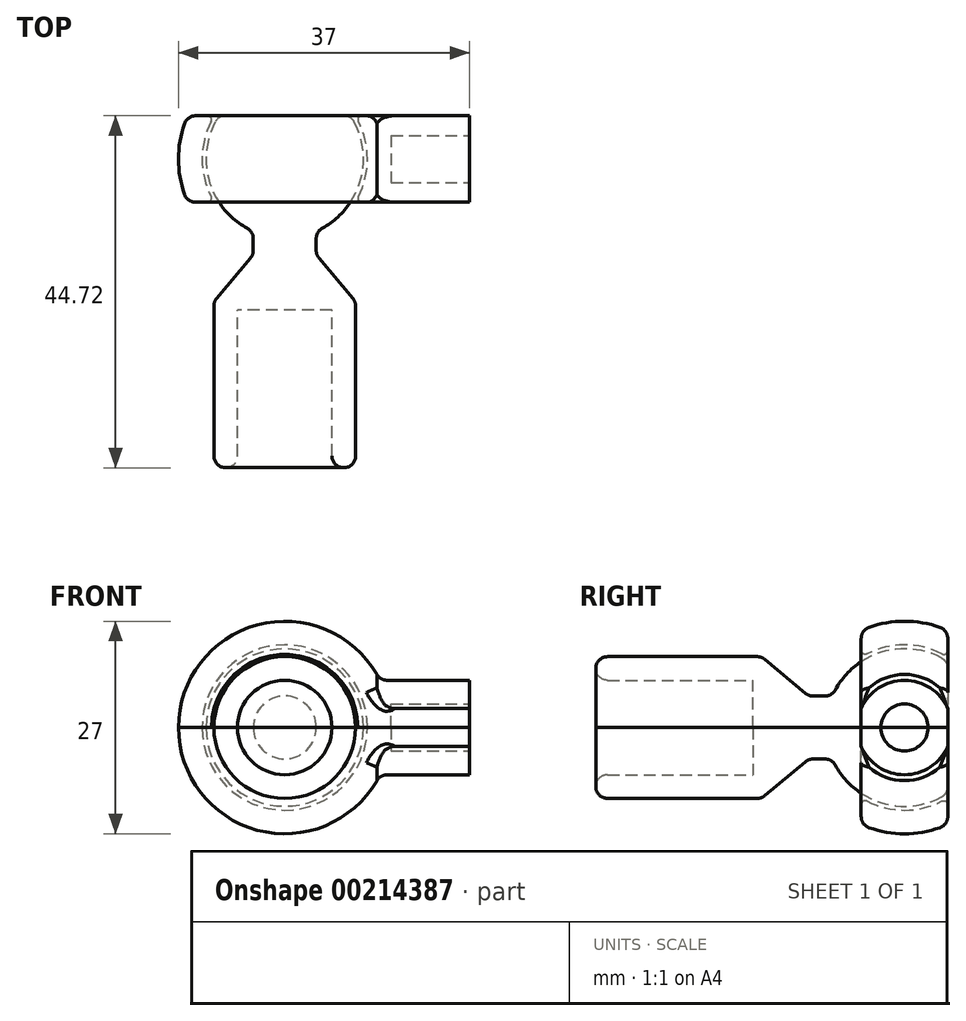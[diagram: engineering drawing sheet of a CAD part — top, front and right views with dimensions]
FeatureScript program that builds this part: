
annotation { "Feature Type Name" : "Feature", "Feature Type Description" : "" }
export const myFeature = defineFeature(function(context is Context, id is Id, definition is map)
    precondition{}
    {
        {
            var Q0;
            Q0=qCreatedBy(makeId("Top.planeOp"),FACE);
            var sketch = newSketch(context, id + "F0", { "sketchPlane" : qUnion([Q0])});
            skArc(sketch, "E0", {"start": v(-8.35, 5.5) * mm, "mid": v(-9.59, -2.84) * mm, "end": v(-4, -9.17) * mm});
            skLineSegment(sketch, "E1", {"start": v(-8.35, 5.5) * mm, "end": v(0, 5.5) * mm});
            skLineSegment(sketch, "E2", {"start": v(0, 14.58) * mm, "end": v(0, -45.08) * mm, "construction": true});
            skLineSegment(sketch, "E3", {"start": v(-4, -9.17) * mm, "end": v(-4, -12.17) * mm});
            skLineSegment(sketch, "E4", {"start": v(-4, -12.17) * mm, "end": v(-9, -18.12) * mm});
            skLineSegment(sketch, "E5", {"start": v(-9, -18.12) * mm, "end": v(-9, -39.22) * mm});
            skLineSegment(sketch, "E6", {"start": v(-9, -39.22) * mm, "end": v(-6, -39.22) * mm});
            skLineSegment(sketch, "E7", {"start": v(-6, -39.22) * mm, "end": v(-6, -19.22) * mm});
            skLineSegment(sketch, "E8", {"start": v(-6, -19.22) * mm, "end": v(0, -19.22) * mm});
            skLineSegment(sketch, "E9", {"start": v(-6, -19.22) * mm, "end": v(-8.3, -17.29) * mm, "construction": true});
            skPoint(sketch, "E10.MirrorCS.end.orphan", {"position": v(0, -19.22) * mm});
            skPoint(sketch, "E10.MirrorCS.start.orphan", {"position": v(6, -19.22) * mm});
            skPoint(sketch, "E11.MirrorCS.start.orphan", {"position": v(6, -39.22) * mm});
            skPoint(sketch, "E12.MirrorCS.start.orphan", {"position": v(9, -39.22) * mm});
            skPoint(sketch, "E13.MirrorCS.start.orphan", {"position": v(9, -18.12) * mm});
            skPoint(sketch, "E14.MirrorCS.start.orphan", {"position": v(4, -12.17) * mm});
            skPoint(sketch, "E15.MirrorCS.start.orphan", {"position": v(4, -9.17) * mm});
            skPoint(sketch, "E16.MirrorCS.start.orphan", {"position": v(8.35, 5.5) * mm});
            skPoint(sketch, "E17.MirrorCS.end.orphan", {"position": v(0, 5.5) * mm});
            skLineSegment(sketch, "E18", {"start": v(0, -19.22) * mm, "end": v(0, 5.5) * mm});
            skSolve(sketch);
        }
        {
            var Q0;
            Q0 = qSketchRegion(id + "F0", true);
            var Q1;
            Q1=sQuery(id+"F0.wireOp",EDGE,"E2");
            revolve(context, id + "F1", {"entities" : qUnion([Q0]), "axis" : qUnion([Q1]), "revolveType" : RevolveType.ONE_DIRECTION, "angle" : 180 * degree});
        }
        {
            var Q0;
            Q0=makeQuery(id+"F1.opRevolve","SWEPT_EDGE",EDGE,{"disambiguationData":[OSD([sQuery(id+"F0.wireOp",EDGE,"E0"),sQuery(id+"F0.wireOp",EDGE,"E3")])]});
            var Q1;
            Q1=makeQuery(id+"F1.opRevolve","SWEPT_EDGE",EDGE,{"disambiguationData":[OSD([sQuery(id+"F0.wireOp",EDGE,"E3"),sQuery(id+"F0.wireOp",EDGE,"E4")])]});
            var Q2;
            Q2=makeQuery(id+"F1.opRevolve","SWEPT_EDGE",EDGE,{"disambiguationData":[OSD([sQuery(id+"F0.wireOp",EDGE,"E4"),sQuery(id+"F0.wireOp",EDGE,"E5")])]});
            var Q3;
            Q3=makeQuery(id+"F1.opRevolve","SWEPT_EDGE",EDGE,{"disambiguationData":[OSD([sQuery(id+"F0.wireOp",EDGE,"E5"),sQuery(id+"F0.wireOp",EDGE,"E6")])]});
            var Q4;
            Q4=makeQuery(id+"F1.opRevolve","SWEPT_EDGE",EDGE,{"disambiguationData":[OSD([sQuery(id+"F0.wireOp",EDGE,"E6"),sQuery(id+"F0.wireOp",EDGE,"E7")])]});
            var Q5;
            Q5=makeQuery(id+"F1.opRevolve","SWEPT_EDGE",EDGE,{"disambiguationData":[OSD([sQuery(id+"F0.wireOp",EDGE,"E0"),sQuery(id+"F0.wireOp",EDGE,"E1")])]});
            fillet(context, id + "F2", {"entities" : qUnion([Q0, Q1, Q2, Q3, Q4, Q5]), "radius" : 1.5 * mm, "tangentPropagation" : true, "allowEdgeOverflow" : false});
        }
        {
            var Q0;
            Q0=makeQuery(id+"F1.opRevolve","CAP_FACE",FACE,{"disambiguationData":[OSD([sQuery(id+"F0.wireOp",EDGE,"E0"),sQuery(id+"F0.wireOp",EDGE,"E1"),sQuery(id+"F0.wireOp",EDGE,"E3"),sQuery(id+"F0.wireOp",EDGE,"E4"),sQuery(id+"F0.wireOp",EDGE,"E5"),sQuery(id+"F0.wireOp",EDGE,"E6"),sQuery(id+"F0.wireOp",EDGE,"E7"),sQuery(id+"F0.wireOp",EDGE,"E8"),sQuery(id+"F0.wireOp",EDGE,"E18")])],"isStart":true});
            var sketch = newSketch(context, id + "F3", { "sketchPlane" : qUnion([Q0])});
            skArc(sketch, "E19", {"start": v(8.94, -5.5) * mm, "mid": v(10.5, 0) * mm, "end": v(8.94, 5.5) * mm});
            skArc(sketch, "E20", {"start": v(12.33, -5.5) * mm, "mid": v(13.5, 0) * mm, "end": v(12.33, 5.5) * mm});
            skLineSegment(sketch, "E21", {"start": v(0, 0) * mm, "end": v(17.84, 0) * mm, "construction": true});
            skLineSegment(sketch, "E22", {"start": v(12.33, 5.5) * mm, "end": v(8.94, 5.5) * mm});
            skLineSegment(sketch, "E23.MirrorCS", {"start": v(12.33, -5.5) * mm, "end": v(8.94, -5.5) * mm});
            skLineSegment(sketch, "E24", {"start": v(0, 0) * mm, "end": v(0, -5) * mm, "construction": true});
            skPoint(sketch, "E25.orphan", {"position": v(14.47, -5.5) * mm});
            skPoint(sketch, "E26.orphan", {"position": v(14.47, 5.5) * mm});
            skPoint(sketch, "E27.trimOffspring.end.orphan", {"position": v(-16.23, -5) * mm});
            skPoint(sketch, "E28.trimOffspring.end.orphan", {"position": v(-16.23, 5) * mm});
            skSolve(sketch);
        }
        {
            var Q0;
            Q0 = qSketchRegion(id + "F3", true);
            var Q1;
            Q1=sQuery(id+"F3.wireOp",EDGE,"E24");
            revolve(context, id + "F4", {"entities" : qUnion([Q0]), "axis" : qUnion([Q1]), "revolveType" : RevolveType.ONE_DIRECTION, "angle" : 180 * degree});
        }
        {
            var Q0;
            Q0=makeQuery(id+"F1.opRevolve","SWEPT_BODY",BODY,{"disambiguationData":[OSD([sQuery(id+"F0.wireOp",EDGE,"E0"),sQuery(id+"F0.wireOp",EDGE,"E1"),sQuery(id+"F0.wireOp",EDGE,"E3"),sQuery(id+"F0.wireOp",EDGE,"E4"),sQuery(id+"F0.wireOp",EDGE,"E5"),sQuery(id+"F0.wireOp",EDGE,"E6"),sQuery(id+"F0.wireOp",EDGE,"E7"),sQuery(id+"F0.wireOp",EDGE,"E8"),sQuery(id+"F0.wireOp",EDGE,"E18")])]});
            var Q1;
            Q1=makeQuery(id+"F1.opRevolve","CAP_FACE",FACE,{"disambiguationData":[OSD([sQuery(id+"F0.wireOp",EDGE,"E0"),sQuery(id+"F0.wireOp",EDGE,"E1"),sQuery(id+"F0.wireOp",EDGE,"E3"),sQuery(id+"F0.wireOp",EDGE,"E4"),sQuery(id+"F0.wireOp",EDGE,"E5"),sQuery(id+"F0.wireOp",EDGE,"E6"),sQuery(id+"F0.wireOp",EDGE,"E7"),sQuery(id+"F0.wireOp",EDGE,"E8"),sQuery(id+"F0.wireOp",EDGE,"E18")])],"isStart":true});
            mirror(context, id + "F5", {"operationType" : NewBodyOperationType.ADD, "entities" : qUnion([Q0]), "mirrorPlane" : qUnion([Q1])});
        }
        {
            var Q0;
            Q0=makeQuery(id+"F4.opRevolve","CAP_FACE",FACE,{"disambiguationData":[OSD([sQuery(id+"F3.wireOp",EDGE,"E19"),sQuery(id+"F3.wireOp",EDGE,"E20"),sQuery(id+"F3.wireOp",EDGE,"E22"),sQuery(id+"F3.wireOp",EDGE,"E23.MirrorCS")])],"isStart":true});
            var sketch = newSketch(context, id + "F6", { "sketchPlane" : qUnion([Q0])});
            skLineSegment(sketch, "E29.bottom", {"start": v(10.5, 0) * mm, "end": v(13.5, 0) * mm});
            skLineSegment(sketch, "E29.top", {"start": v(10.5, 6) * mm, "end": v(23.5, 6) * mm});
            skLineSegment(sketch, "E29.left", {"start": v(10.5, 0) * mm, "end": v(10.5, 6) * mm});
            skLineSegment(sketch, "E29.right", {"start": v(23.5, 3) * mm, "end": v(23.5, 6) * mm});
            skLineSegment(sketch, "E30", {"start": v(13.5, 0) * mm, "end": v(13.5, 3) * mm});
            skLineSegment(sketch, "E31", {"start": v(13.5, 3) * mm, "end": v(23.5, 3) * mm});
            skSolve(sketch);
        }
        {
            var Q0;
            Q0 = qSketchRegion(id + "F6", true);
            var Q1;
            Q1=sQuery(id+"F6.wireOp",EDGE,"E29.bottom");
            revolve(context, id + "F7", {"entities" : qUnion([Q0]), "axis" : qUnion([Q1]), "revolveType" : RevolveType.ONE_DIRECTION, "oppositeDirection" : true, "angle" : 90 * degree});
        }
        {
            var Q0;
            Q0=makeQuery(id+"F7.opRevolve","SWEPT_FACE",FACE,{"disambiguationData":[OSD([sQuery(id+"F6.wireOp",EDGE,"E29.left")])]});
            var sketch = newSketch(context, id + "F8", { "sketchPlane" : qUnion([Q0])});
            skLineSegment(sketch, "E32.bottom", {"start": v(5.5, 0) * mm, "end": v(8.43, 0) * mm});
            skLineSegment(sketch, "E32.top", {"start": v(5.5, 6.46) * mm, "end": v(8.43, 6.46) * mm});
            skLineSegment(sketch, "E32.left", {"start": v(5.5, 0) * mm, "end": v(5.5, 6.46) * mm});
            skLineSegment(sketch, "E32.right", {"start": v(8.43, 0) * mm, "end": v(8.43, 6.46) * mm});
            skSolve(sketch);
        }
        {
            var Q0;
            {var subQ2=sQuery(id+"F8.wireOp",EDGE,"E32.top");Q0=makeQuery(id+"F8.imprint","IMPRINT",FACE,{"disambiguationData":[TD([[makeQuery(id+"F8.imprint","IMPRINT",EDGE,{"derivedFrom":subQ2}),-1.0]])]});}
            var Q1;
            {var subQ0=sQuery(id+"F8.wireOp",EDGE,"E32.bottom");var subQ1=sQuery(id+"F6.wireOp",EDGE,"E29.left");var subQ2=makeQuery(id+"F7.opRevolve","SWEPT_EDGE",EDGE,{"disambiguationData":[OSD([sQuery(id+"F6.wireOp",EDGE,"E29.top"),subQ1])]});var subQ3=makeQuery(id+"F8.imprint","INTERSECT",VERTEX,{"derivedFrom":[subQ2,subQ0]});Q1=makeQuery(id+"F8.imprint","IMPRINT",FACE,{"disambiguationData":[TD([[makeQuery(id+"F8.imprint","IMPRINT",EDGE,{"disambiguationData":[TD([[subQ3,1.0]])],"derivedFrom":subQ0}),1.0]])]});}
            extrude(context, id + "F9", {"entities" : qUnion([Q0, Q1]), "operationType" : NewBodyOperationType.REMOVE, "oppositeDirection" : true, "depth" : 25 * mm});
        }
        {
            var Q0;
            Q0=makeQuery(id+"F7.opRevolve","SWEPT_BODY",BODY,{"disambiguationData":[OSD([sQuery(id+"F6.wireOp",EDGE,"E29.bottom"),sQuery(id+"F6.wireOp",EDGE,"E29.top"),sQuery(id+"F6.wireOp",EDGE,"E29.left"),sQuery(id+"F6.wireOp",EDGE,"E29.right"),sQuery(id+"F6.wireOp",EDGE,"E30"),sQuery(id+"F6.wireOp",EDGE,"E31")])]});
            var Q1;
            Q1=makeQuery(id+"F7.opRevolve","CAP_FACE",FACE,{"disambiguationData":[OSD([sQuery(id+"F6.wireOp",EDGE,"E29.bottom"),sQuery(id+"F6.wireOp",EDGE,"E29.top"),sQuery(id+"F6.wireOp",EDGE,"E29.left"),sQuery(id+"F6.wireOp",EDGE,"E29.right"),sQuery(id+"F6.wireOp",EDGE,"E30"),sQuery(id+"F6.wireOp",EDGE,"E31")])],"isStart":false});
            mirror(context, id + "F10", {"operationType" : NewBodyOperationType.ADD, "entities" : qUnion([Q0]), "mirrorPlane" : qUnion([Q1])});
        }
        {
            var Q0;
            Q0=makeQuery(id+"F4.opRevolve","SWEPT_BODY",BODY,{"disambiguationData":[OSD([sQuery(id+"F3.wireOp",EDGE,"E19"),sQuery(id+"F3.wireOp",EDGE,"E20"),sQuery(id+"F3.wireOp",EDGE,"E22"),sQuery(id+"F3.wireOp",EDGE,"E23.MirrorCS")])]});
            var Q1;
            {var subQ0=makeQuery(id+"F7.opRevolve","CAP_FACE",FACE,{"disambiguationData":[OSD([sQuery(id+"F6.wireOp",EDGE,"E29.bottom"),sQuery(id+"F6.wireOp",EDGE,"E29.top"),sQuery(id+"F6.wireOp",EDGE,"E29.left"),sQuery(id+"F6.wireOp",EDGE,"E29.right"),sQuery(id+"F6.wireOp",EDGE,"E30"),sQuery(id+"F6.wireOp",EDGE,"E31")])],"isStart":true});Q1=makeQuery(id+"F10.boolean.opBoolean","MERGE",FACE,{"derivedFrom":[makeQuery(id+"F4.opRevolve","CAP_FACE",FACE,{"disambiguationData":[OSD([sQuery(id+"F3.wireOp",EDGE,"E19"),sQuery(id+"F3.wireOp",EDGE,"E20"),sQuery(id+"F3.wireOp",EDGE,"E22"),sQuery(id+"F3.wireOp",EDGE,"E23.MirrorCS")])],"isStart":true}),subQ0,makeQuery(id+"F10.opPattern","COPY",FACE,{"derivedFrom":subQ0,"instanceName":"1"})]});}
            mirror(context, id + "F11", {"operationType" : NewBodyOperationType.ADD, "entities" : qUnion([Q0]), "mirrorPlane" : qUnion([Q1])});
        }
        {
            var Q0;
            {var subQ0=makeQuery(id+"F7.opRevolve","SWEPT_FACE",FACE,{"disambiguationData":[OSD([sQuery(id+"F6.wireOp",EDGE,"E29.top")])]});Q0=makeQuery(id+"F10.boolean.opBoolean","INTERSECT",EDGE,{"derivedFrom":[makeQuery(id+"F4.opRevolve","SWEPT_FACE",FACE,{"disambiguationData":[OSD([sQuery(id+"F3.wireOp",EDGE,"E20")])]}),subQ0,makeQuery(id+"F10.opPattern","COPY",FACE,{"derivedFrom":subQ0,"instanceName":"1"})]});}
            var Q1;
            {var subQ0=makeQuery(id+"F7.opRevolve","SWEPT_FACE",FACE,{"disambiguationData":[OSD([sQuery(id+"F6.wireOp",EDGE,"E29.top")])]});Q1=makeQuery(id+"F11.opPattern","COPY",EDGE,{"derivedFrom":makeQuery(id+"F10.boolean.opBoolean","INTERSECT",EDGE,{"derivedFrom":[makeQuery(id+"F4.opRevolve","SWEPT_FACE",FACE,{"disambiguationData":[OSD([sQuery(id+"F3.wireOp",EDGE,"E20")])]}),subQ0,makeQuery(id+"F10.opPattern","COPY",FACE,{"derivedFrom":subQ0,"instanceName":"1"})]}),"instanceName":"1"});}
            var Q2;
            {var subQ0=makeQuery(id+"F4.opRevolve","SWEPT_EDGE",EDGE,{"disambiguationData":[OSD([sQuery(id+"F3.wireOp",EDGE,"E20"),sQuery(id+"F3.wireOp",EDGE,"E22")])]});Q2=makeQuery(id+"F11.boolean.opBoolean","MERGE",EDGE,{"derivedFrom":[subQ0,makeQuery(id+"F11.opPattern","COPY",EDGE,{"derivedFrom":subQ0,"instanceName":"1"})]});}
            var Q3;
            {var subQ0=makeQuery(id+"F4.opRevolve","SWEPT_EDGE",EDGE,{"disambiguationData":[OSD([sQuery(id+"F3.wireOp",EDGE,"E20"),sQuery(id+"F3.wireOp",EDGE,"E23.MirrorCS")])]});Q3=makeQuery(id+"F11.boolean.opBoolean","MERGE",EDGE,{"derivedFrom":[subQ0,makeQuery(id+"F11.opPattern","COPY",EDGE,{"derivedFrom":subQ0,"instanceName":"1"})]});}
            fillet(context, id + "F12", {"entities" : qUnion([Q0, Q1, Q2, Q3]), "radius" : 1.5 * mm, "tangentPropagation" : true, "allowEdgeOverflow" : false});
        }
        {
            var Q0;
            {var subQ0=makeQuery(id+"F4.opRevolve","SWEPT_EDGE",EDGE,{"disambiguationData":[OSD([sQuery(id+"F3.wireOp",EDGE,"E19"),sQuery(id+"F3.wireOp",EDGE,"E23.MirrorCS")])]});Q0=makeQuery(id+"F11.boolean.opBoolean","MERGE",EDGE,{"derivedFrom":[subQ0,makeQuery(id+"F11.opPattern","COPY",EDGE,{"derivedFrom":subQ0,"instanceName":"1"})]});}
            var Q1;
            {var subQ0=makeQuery(id+"F4.opRevolve","SWEPT_EDGE",EDGE,{"disambiguationData":[OSD([sQuery(id+"F3.wireOp",EDGE,"E19"),sQuery(id+"F3.wireOp",EDGE,"E22")])]});Q1=makeQuery(id+"F11.boolean.opBoolean","MERGE",EDGE,{"derivedFrom":[subQ0,makeQuery(id+"F11.opPattern","COPY",EDGE,{"derivedFrom":subQ0,"instanceName":"1"})]});}
            fillet(context, id + "F13", {"entities" : qUnion([Q0, Q1]), "radius" : 0.5 * mm, "tangentPropagation" : true, "allowEdgeOverflow" : false});
        }
    });
